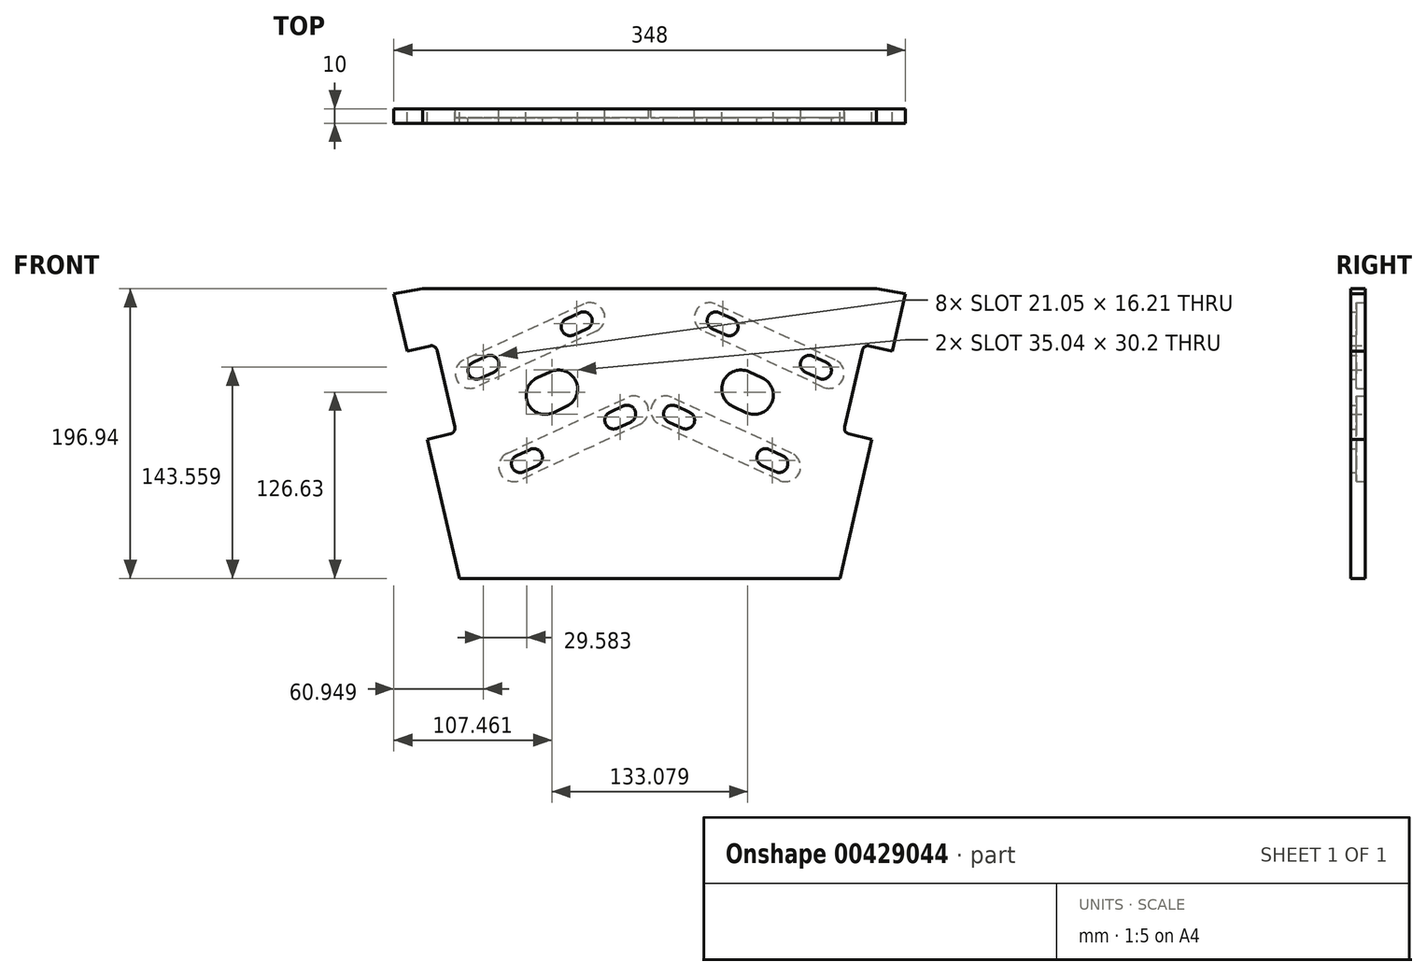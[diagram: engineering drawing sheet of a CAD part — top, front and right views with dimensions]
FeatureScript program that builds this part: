
annotation { "Feature Type Name" : "Feature", "Feature Type Description" : "" }
export const myFeature = defineFeature(function(context is Context, id is Id, definition is map)
    precondition{}
    {
        {
            var Q0;
            Q0=qCreatedBy(makeId("Front.planeOp"),FACE);
            var sketch = newSketch(context, id + "F0", { "sketchPlane" : qUnion([Q0])});
            skLineSegment(sketch, "E0", {"start": v(-89.77, 99.21) * mm, "end": v(-204.19, 99.21) * mm});
            skLineSegment(sketch, "E1", {"start": v(-179.25, -97.73) * mm, "end": v(-49.92, -97.73) * mm});
            skArc(sketch, "E2", {"start": v(-140.46, -14.29) * mm, "mid": v(-143.36, -22.26) * mm, "end": v(-135.38, -25.16) * mm});
            skArc(sketch, "E3", {"start": v(-126.32, -20.94) * mm, "mid": v(-123.42, -12.96) * mm, "end": v(-131.4, -10.06) * mm});
            skLineSegment(sketch, "E4", {"start": v(-140.46, -14.29) * mm, "end": v(-131.4, -10.06) * mm});
            skLineSegment(sketch, "E5", {"start": v(-135.38, -25.16) * mm, "end": v(-126.32, -20.94) * mm});
            skArc(sketch, "E6.MirrorCS", {"start": v(-71.94, 4.42) * mm, "mid": v(-79.92, 7.32) * mm, "end": v(-77.01, 15.3) * mm});
            skLineSegment(sketch, "E7.MirrorCS", {"start": v(-62.88, 8.65) * mm, "end": v(-71.94, 4.42) * mm});
            skLineSegment(sketch, "E8.MirrorCS", {"start": v(-67.95, 19.52) * mm, "end": v(-77.01, 15.3) * mm});
            skArc(sketch, "E9.MirrorCS", {"start": v(-67.95, 19.52) * mm, "mid": v(-59.98, 16.62) * mm, "end": v(-62.88, 8.65) * mm});
            skLineSegment(sketch, "E10", {"start": v(-142.19, -10.57) * mm, "end": v(-69.68, 23.24) * mm});
            skLineSegment(sketch, "E11", {"start": v(-133.65, -28.88) * mm, "end": v(-61.15, 4.93) * mm});
            skArc(sketch, "E12", {"start": v(-56.61, 7.04) * mm, "mid": v(-51.73, 20.47) * mm, "end": v(-65.15, 25.35) * mm});
            skLineSegment(sketch, "E13", {"start": v(-69.68, 23.24) * mm, "end": v(-65.15, 25.35) * mm});
            skLineSegment(sketch, "E14", {"start": v(-61.15, 4.93) * mm, "end": v(-56.61, 7.04) * mm});
            skArc(sketch, "E15.MirrorCS", {"start": v(-138.18, -31) * mm, "mid": v(-151.6, -26.1) * mm, "end": v(-146.72, -12.68) * mm});
            skLineSegment(sketch, "E16.MirrorCS", {"start": v(-142.19, -10.57) * mm, "end": v(-146.72, -12.68) * mm});
            skLineSegment(sketch, "E17.MirrorCS", {"start": v(-133.65, -28.88) * mm, "end": v(-138.18, -31) * mm});
            skLineSegment(sketch, "E18.MirrorCS", {"start": v(-163.23, 34.56) * mm, "end": v(-90.73, 68.37) * mm});
            skLineSegment(sketch, "E19.MirrorCS", {"start": v(-171.77, 52.87) * mm, "end": v(-99.27, 86.68) * mm});
            skArc(sketch, "E20.MirrorCS", {"start": v(-176.3, 50.76) * mm, "mid": v(-181.19, 37.33) * mm, "end": v(-167.77, 32.45) * mm});
            skLineSegment(sketch, "E21.MirrorCS", {"start": v(-163.23, 34.56) * mm, "end": v(-167.77, 32.45) * mm});
            skLineSegment(sketch, "E22.MirrorCS", {"start": v(-171.77, 52.87) * mm, "end": v(-176.3, 50.76) * mm});
            skLineSegment(sketch, "E23.MirrorCS", {"start": v(-90.73, 68.37) * mm, "end": v(-86.2, 70.48) * mm});
            skLineSegment(sketch, "E24.MirrorCS", {"start": v(-99.27, 86.68) * mm, "end": v(-94.74, 88.8) * mm});
            skArc(sketch, "E25.MirrorCS", {"start": v(-94.74, 88.8) * mm, "mid": v(-81.31, 83.9) * mm, "end": v(-86.2, 70.48) * mm});
            skLineSegment(sketch, "E26.MirrorCS", {"start": v(-164.97, 38.28) * mm, "end": v(-155.9, 42.5) * mm});
            skArc(sketch, "E27.MirrorCS", {"start": v(-160.98, 53.38) * mm, "mid": v(-153, 50.48) * mm, "end": v(-155.9, 42.5) * mm});
            skLineSegment(sketch, "E28.MirrorCS", {"start": v(-170.04, 49.15) * mm, "end": v(-160.98, 53.38) * mm});
            skArc(sketch, "E29.MirrorCS", {"start": v(-164.97, 38.28) * mm, "mid": v(-172.94, 41.18) * mm, "end": v(-170.04, 49.15) * mm});
            skArc(sketch, "E30.MirrorCS", {"start": v(-92.46, 72.09) * mm, "mid": v(-89.56, 80.06) * mm, "end": v(-97.53, 82.96) * mm});
            skLineSegment(sketch, "E31.MirrorCS", {"start": v(-97.53, 82.96) * mm, "end": v(-106.6, 78.74) * mm});
            skLineSegment(sketch, "E32.MirrorCS", {"start": v(-92.46, 72.09) * mm, "end": v(-101.53, 67.86) * mm});
            skArc(sketch, "E33.MirrorCS", {"start": v(-106.6, 78.74) * mm, "mid": v(-109.5, 70.76) * mm, "end": v(-101.53, 67.86) * mm});
            skArc(sketch, "E34", {"start": v(-126.48, 38.57) * mm, "mid": v(-132.77, 21.3) * mm, "end": v(-115.5, 15) * mm});
            skLineSegment(sketch, "E35", {"start": v(-126.48, 38.57) * mm, "end": v(-117.42, 42.8) * mm});
            skLineSegment(sketch, "E36", {"start": v(-115.5, 15) * mm, "end": v(-106.43, 19.23) * mm});
            skArc(sketch, "E37.trimOffspring", {"start": v(-106.43, 19.23) * mm, "mid": v(-100.15, 36.5) * mm, "end": v(-117.42, 42.8) * mm});
            skLineSegment(sketch, "E38", {"start": v(-223.92, 95.78) * mm, "end": v(-214.92, 56.8) * mm});
            skLineSegment(sketch, "E39", {"start": v(-194.53, 57.4) * mm, "end": v(-182.5, 5.27) * mm});
            skLineSegment(sketch, "E40", {"start": v(-204.19, 99.21) * mm, "end": v(-223.92, 95.78) * mm});
            skLineSegment(sketch, "E41", {"start": v(-214.92, 56.8) * mm, "end": v(-199.33, 60.4) * mm});
            skLineSegment(sketch, "E42", {"start": v(-201.09, -3.12) * mm, "end": v(-185.5, 0.48) * mm});
            skLineSegment(sketch, "E43.MirrorCS", {"start": v(-2.3, 82.96) * mm, "end": v(6.76, 78.74) * mm});
            skLineSegment(sketch, "E44.MirrorCS", {"start": v(33.81, -28.88) * mm, "end": v(38.34, -31) * mm});
            skLineSegment(sketch, "E45.MirrorCS", {"start": v(-7.38, 72.09) * mm, "end": v(1.69, 67.86) * mm});
            skLineSegment(sketch, "E46.MirrorCS", {"start": v(71.93, 52.87) * mm, "end": v(76.46, 50.76) * mm});
            skLineSegment(sketch, "E47.MirrorCS", {"start": v(-31.89, 19.52) * mm, "end": v(-22.83, 15.3) * mm});
            skLineSegment(sketch, "E48.MirrorCS", {"start": v(63.4, 34.56) * mm, "end": v(67.93, 32.45) * mm});
            skLineSegment(sketch, "E49.MirrorCS", {"start": v(15.66, 15) * mm, "end": v(6.6, 19.23) * mm});
            skLineSegment(sketch, "E50.MirrorCS", {"start": v(35.54, -25.16) * mm, "end": v(26.48, -20.94) * mm});
            skLineSegment(sketch, "E51.MirrorCS", {"start": v(65.13, 38.28) * mm, "end": v(56.07, 42.5) * mm});
            skLineSegment(sketch, "E52.MirrorCS", {"start": v(-36.96, 8.65) * mm, "end": v(-27.9, 4.42) * mm});
            skLineSegment(sketch, "E53.MirrorCS", {"start": v(-9.1, 68.37) * mm, "end": v(-13.64, 70.48) * mm});
            skLineSegment(sketch, "E54.MirrorCS", {"start": v(-38.7, 4.93) * mm, "end": v(-43.22, 7.04) * mm});
            skLineSegment(sketch, "E55.MirrorCS", {"start": v(70.2, 49.15) * mm, "end": v(61.14, 53.38) * mm});
            skLineSegment(sketch, "E56.MirrorCS", {"start": v(26.65, 38.57) * mm, "end": v(17.58, 42.8) * mm});
            skLineSegment(sketch, "E57.MirrorCS", {"start": v(-0.57, 86.68) * mm, "end": v(-5.1, 88.8) * mm});
            skLineSegment(sketch, "E58.MirrorCS", {"start": v(40.62, -14.29) * mm, "end": v(31.55, -10.06) * mm});
            skLineSegment(sketch, "E59.MirrorCS", {"start": v(-30.16, 23.24) * mm, "end": v(-34.69, 25.35) * mm});
            skLineSegment(sketch, "E60.MirrorCS", {"start": v(42.35, -10.57) * mm, "end": v(46.88, -12.68) * mm});
            skArc(sketch, "E61.MirrorCS", {"start": v(-7.38, 72.09) * mm, "mid": v(-10.28, 80.06) * mm, "end": v(-2.3, 82.96) * mm});
            skArc(sketch, "E62.MirrorCS", {"start": v(-31.89, 19.52) * mm, "mid": v(-39.86, 16.62) * mm, "end": v(-36.96, 8.65) * mm});
            skLineSegment(sketch, "E63.MirrorCS", {"start": v(-10.07, 99.21) * mm, "end": v(104.35, 99.21) * mm});
            skArc(sketch, "E64.MirrorCS", {"start": v(65.13, 38.28) * mm, "mid": v(73.1, 41.18) * mm, "end": v(70.2, 49.15) * mm});
            skArc(sketch, "E65.MirrorCS", {"start": v(40.62, -14.29) * mm, "mid": v(43.52, -22.26) * mm, "end": v(35.54, -25.16) * mm});
            skLineSegment(sketch, "E66.MirrorCS", {"start": v(42.35, -10.57) * mm, "end": v(-30.16, 23.24) * mm});
            skArc(sketch, "E67.MirrorCS", {"start": v(-5.1, 88.8) * mm, "mid": v(-18.53, 83.9) * mm, "end": v(-13.64, 70.48) * mm});
            skLineSegment(sketch, "E68.MirrorCS", {"start": v(124.08, 95.78) * mm, "end": v(115.08, 56.8) * mm});
            skLineSegment(sketch, "E69.MirrorCS", {"start": v(63.4, 34.56) * mm, "end": v(-9.1, 68.37) * mm});
            skLineSegment(sketch, "E70.MirrorCS", {"start": v(33.81, -28.88) * mm, "end": v(-38.7, 4.93) * mm});
            skLineSegment(sketch, "E71.MirrorCS", {"start": v(104.35, 99.21) * mm, "end": v(-10.07, 99.21) * mm});
            skArc(sketch, "E72.MirrorCS", {"start": v(6.6, 19.23) * mm, "mid": v(0.3, 36.5) * mm, "end": v(17.58, 42.8) * mm});
            skLineSegment(sketch, "E73.MirrorCS", {"start": v(104.35, 99.21) * mm, "end": v(124.08, 95.78) * mm});
            skArc(sketch, "E74.MirrorCS", {"start": v(6.76, 78.74) * mm, "mid": v(9.66, 70.76) * mm, "end": v(1.69, 67.86) * mm});
            skArc(sketch, "E75.MirrorCS", {"start": v(-43.22, 7.04) * mm, "mid": v(-48.1, 20.47) * mm, "end": v(-34.69, 25.35) * mm});
            skArc(sketch, "E76.MirrorCS", {"start": v(38.34, -31) * mm, "mid": v(51.77, -26.1) * mm, "end": v(46.88, -12.68) * mm});
            skArc(sketch, "E77.MirrorCS", {"start": v(-27.9, 4.42) * mm, "mid": v(-19.92, 7.32) * mm, "end": v(-22.83, 15.3) * mm});
            skArc(sketch, "E78.MirrorCS", {"start": v(61.14, 53.38) * mm, "mid": v(53.16, 50.48) * mm, "end": v(56.07, 42.5) * mm});
            skLineSegment(sketch, "E79.MirrorCS", {"start": v(71.93, 52.87) * mm, "end": v(-0.57, 86.68) * mm});
            skLineSegment(sketch, "E80.MirrorCS", {"start": v(94.7, 57.4) * mm, "end": v(82.66, 5.27) * mm});
            skLineSegment(sketch, "E81.MirrorCS", {"start": v(115.08, 56.8) * mm, "end": v(99.5, 60.4) * mm});
            skArc(sketch, "E82.MirrorCS", {"start": v(26.65, 38.57) * mm, "mid": v(32.93, 21.3) * mm, "end": v(15.66, 15) * mm});
            skLineSegment(sketch, "E83.MirrorCS", {"start": v(101.25, -3.12) * mm, "end": v(85.66, 0.48) * mm});
            skArc(sketch, "E84.MirrorCS", {"start": v(26.48, -20.94) * mm, "mid": v(23.58, -12.96) * mm, "end": v(31.55, -10.06) * mm});
            skArc(sketch, "E85.MirrorCS", {"start": v(76.46, 50.76) * mm, "mid": v(81.35, 37.33) * mm, "end": v(67.93, 32.45) * mm});
            skLineSegment(sketch, "E86", {"start": v(-201.09, -3.12) * mm, "end": v(-179.25, -97.73) * mm});
            skLineSegment(sketch, "E87.MirrorCS", {"start": v(101.25, -3.12) * mm, "end": v(79.4, -97.73) * mm});
            skLineSegment(sketch, "E88.MirrorCS", {"start": v(79.4, -97.73) * mm, "end": v(-49.92, -97.73) * mm});
            skPoint(sketch, "E89.visualSharp", {"position": v(-195.43, 61.3) * mm});
            skArc(sketch, "E89.filletArc", {"start": v(-194.53, 57.4) * mm, "mid": v(-196.31, 59.9) * mm, "end": v(-199.33, 60.4) * mm});
            skPoint(sketch, "E90.visualSharp", {"position": v(-181.6, 1.38) * mm});
            skArc(sketch, "E90.filletArc", {"start": v(-185.5, 0.48) * mm, "mid": v(-183, 2.25) * mm, "end": v(-182.5, 5.27) * mm});
            skPoint(sketch, "E91.visualSharp", {"position": v(95.6, 61.3) * mm});
            skArc(sketch, "E91.filletArc", {"start": v(99.5, 60.4) * mm, "mid": v(96.47, 59.9) * mm, "end": v(94.7, 57.4) * mm});
            skPoint(sketch, "E92.visualSharp", {"position": v(81.76, 1.38) * mm});
            skArc(sketch, "E92.filletArc", {"start": v(82.66, 5.27) * mm, "mid": v(83.17, 2.25) * mm, "end": v(85.66, 0.48) * mm});
            skLineSegment(sketch, "E93", {"start": v(-89.77, 99.21) * mm, "end": v(-10.07, 99.21) * mm});
            skSolve(sketch);
        }
        {
            var Q0;
            Q0 = qSketchRegion(id + "F0", true);
            extrude(context, id + "F1", {"entities" : qUnion([Q0]), "depth" : 10 * mm});
        }
        {
            var Q0;
            Q0=makeQuery(id+"F0.imprint","IMPRINT",FACE,{"disambiguationData":[TD([[makeQuery(id+"F0.imprint","IMPRINT",EDGE,{"derivedFrom":sQuery(id+"F0.wireOp",EDGE,"E18.MirrorCS")}),1.0]])]});
            var Q1;
            Q1=makeQuery(id+"F0.imprint","IMPRINT",FACE,{"disambiguationData":[TD([[makeQuery(id+"F0.imprint","IMPRINT",EDGE,{"derivedFrom":sQuery(id+"F0.wireOp",EDGE,"E43.MirrorCS")}),1.0]])]});
            var Q2;
            Q2=makeQuery(id+"F0.imprint","IMPRINT",FACE,{"disambiguationData":[TD([[makeQuery(id+"F0.imprint","IMPRINT",EDGE,{"derivedFrom":sQuery(id+"F0.wireOp",EDGE,"E2")}),-1.0]])]});
            var Q3;
            Q3=makeQuery(id+"F0.imprint","IMPRINT",FACE,{"disambiguationData":[TD([[makeQuery(id+"F0.imprint","IMPRINT",EDGE,{"derivedFrom":sQuery(id+"F0.wireOp",EDGE,"E44.MirrorCS")}),1.0]])]});
            extrude(context, id + "F2", {"entities" : qUnion([Q0, Q1, Q2, Q3]), "operationType" : NewBodyOperationType.ADD, "depth" : 10 * mm, "hasSecondDirection" : true, "secondDirectionOppositeDirection" : true, "secondDirectionDepth" : -6.1 * mm});
        }
    });
